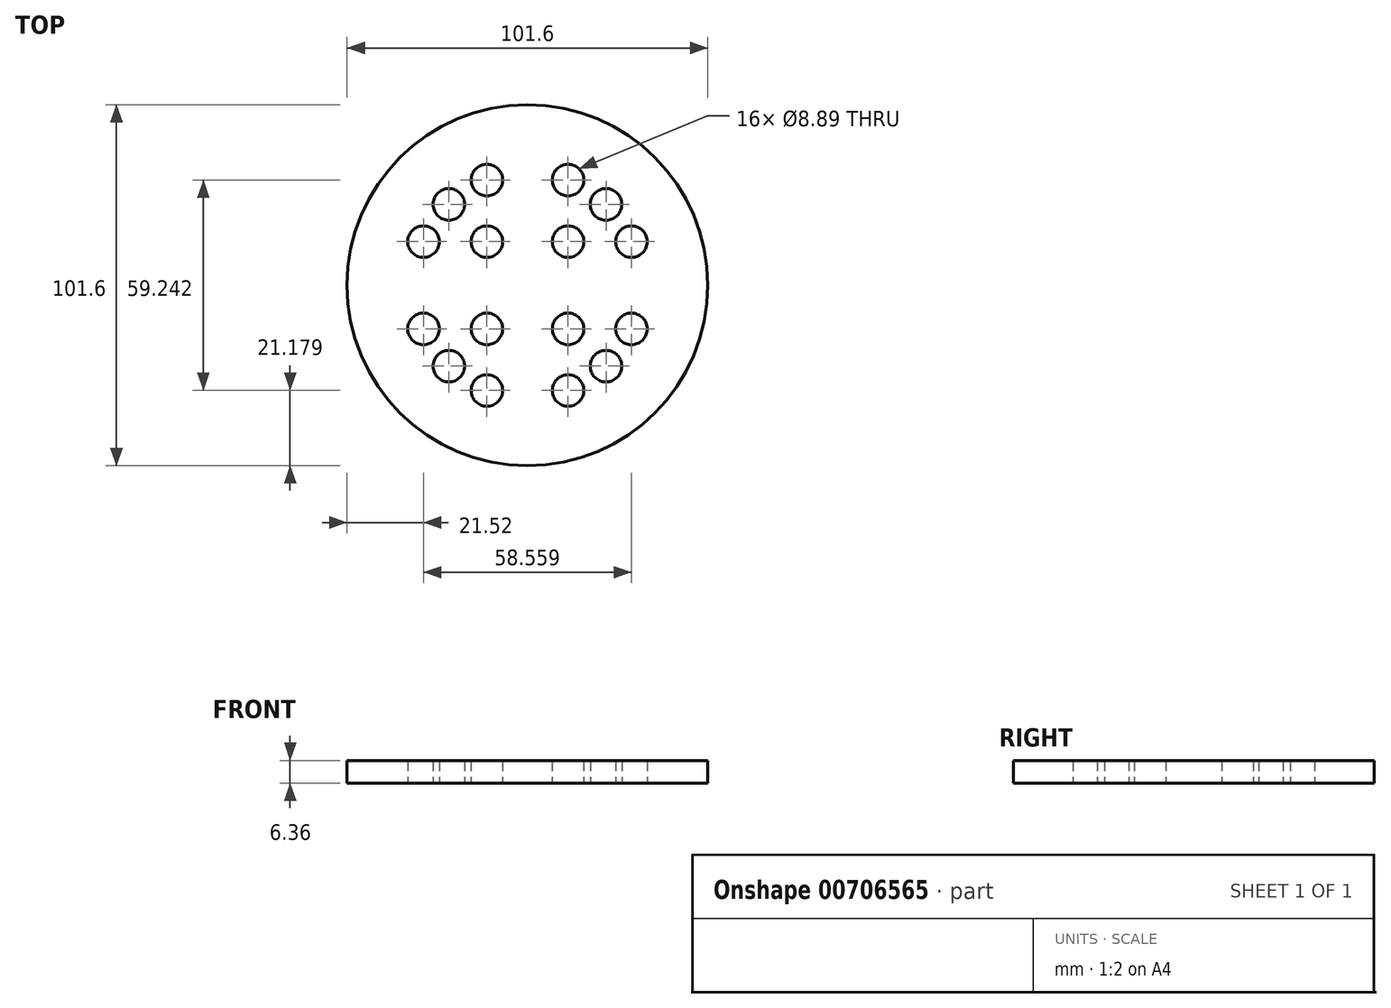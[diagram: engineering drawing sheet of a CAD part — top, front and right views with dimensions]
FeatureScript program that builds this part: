
annotation { "Feature Type Name" : "Feature", "Feature Type Description" : "" }
export const myFeature = defineFeature(function(context is Context, id is Id, definition is map)
    precondition{}
    {
        {
            var Q0;
            Q0=qCreatedBy(makeId("Top.planeOp"),FACE);
            var sketch = newSketch(context, id + "F0", { "sketchPlane" : qUnion([Q0])});
            skCircle(sketch, "E0", {"center": v(0, 0) * mm, "radius": 50.8 * mm});
            skCircle(sketch, "E1", {"center": v(0, 0) * mm, "radius": 31.75 * mm, "construction": true});
            skPoint(sketch, "E2", {"position": v(-11.43, 29.62) * mm});
            skPoint(sketch, "E3", {"position": v(-22.12, 22.77) * mm});
            skPoint(sketch, "E4", {"position": v(-29.28, 12.28) * mm});
            skCircle(sketch, "E5", {"center": v(-29.28, 12.28) * mm, "radius": 4.45 * mm});
            skCircle(sketch, "E6", {"center": v(-22.12, 22.77) * mm, "radius": 4.45 * mm});
            skCircle(sketch, "E7", {"center": v(-11.43, 29.62) * mm, "radius": 4.45 * mm});
            skCircle(sketch, "E8", {"center": v(-11.43, 12.28) * mm, "radius": 4.45 * mm});
            skCircle(sketch, "E9.MirrorC", {"center": v(11.43, 12.28) * mm, "radius": 4.45 * mm});
            skCircle(sketch, "E10.MirrorC", {"center": v(11.43, 29.62) * mm, "radius": 4.45 * mm});
            skCircle(sketch, "E11.MirrorC", {"center": v(22.12, 22.77) * mm, "radius": 4.45 * mm});
            skCircle(sketch, "E12.MirrorC", {"center": v(29.28, 12.28) * mm, "radius": 4.45 * mm});
            skCircle(sketch, "E13.MirrorC", {"center": v(11.43, -12.28) * mm, "radius": 4.45 * mm});
            skCircle(sketch, "E14.MirrorC", {"center": v(29.28, -12.28) * mm, "radius": 4.45 * mm});
            skCircle(sketch, "E15.MirrorC", {"center": v(11.43, -29.62) * mm, "radius": 4.45 * mm});
            skCircle(sketch, "E16.MirrorC", {"center": v(22.12, -22.77) * mm, "radius": 4.45 * mm});
            skCircle(sketch, "E17.MirrorC", {"center": v(-11.43, -12.28) * mm, "radius": 4.45 * mm});
            skCircle(sketch, "E18.MirrorC", {"center": v(-29.28, -12.28) * mm, "radius": 4.45 * mm});
            skCircle(sketch, "E19.MirrorC", {"center": v(-22.12, -22.77) * mm, "radius": 4.45 * mm});
            skCircle(sketch, "E20.MirrorC", {"center": v(-11.43, -29.62) * mm, "radius": 4.45 * mm});
            skSolve(sketch);
        }
        {
            var Q0;
            Q0=makeQuery(id+"F0.imprint","IMPRINT",FACE,{"disambiguationData":[TD([[makeQuery(id+"F0.imprint","IMPRINT",EDGE,{"derivedFrom":sQuery(id+"F0.wireOp",EDGE,"E0")}),1.0]])]});
            extrude(context, id + "F1", {"entities" : qUnion([Q0]), "endBound" : BoundingType.SYMMETRIC, "depth" : 6.35 * mm, "offsetDistance" : 25.4 * mm});
        }
    });
